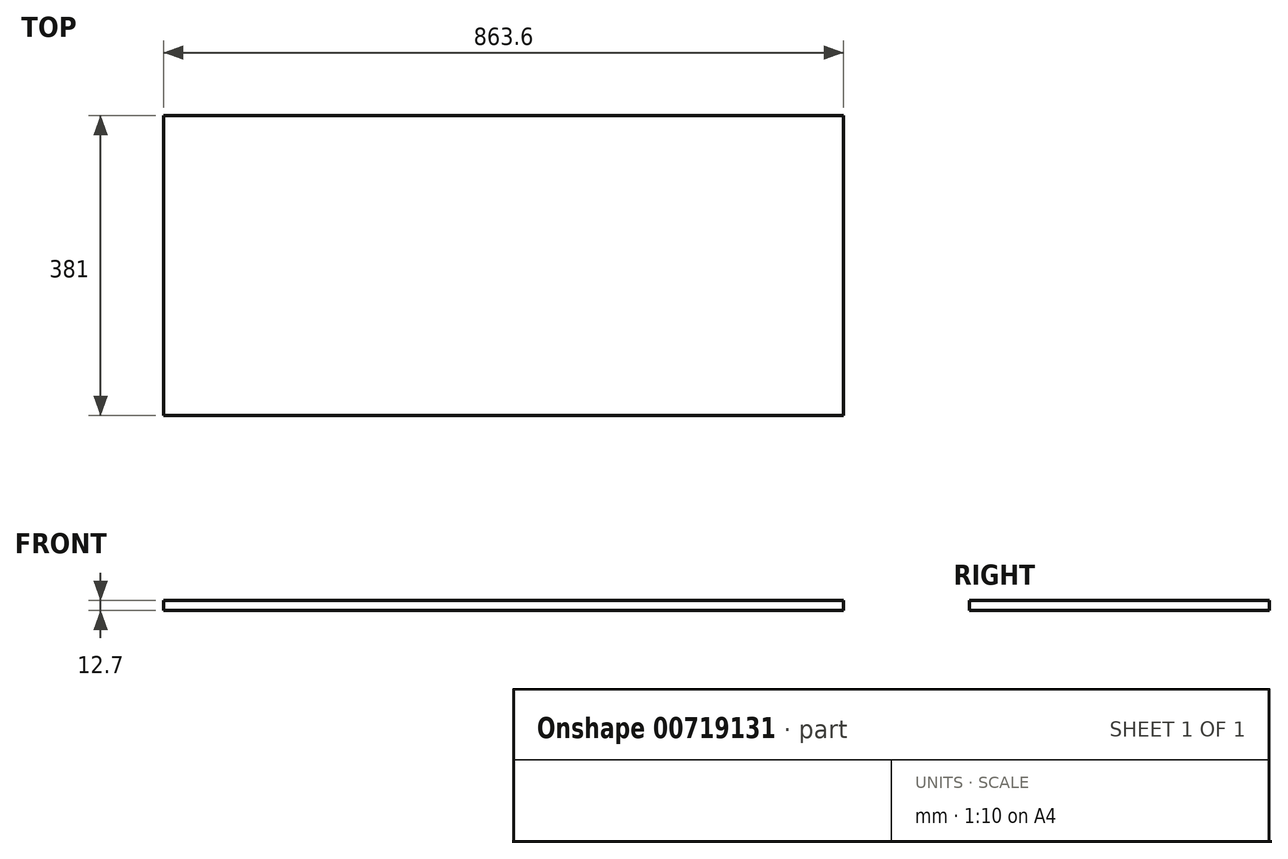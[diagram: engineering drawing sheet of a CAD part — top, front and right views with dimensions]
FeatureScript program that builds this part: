
annotation { "Feature Type Name" : "Feature", "Feature Type Description" : "" }
export const myFeature = defineFeature(function(context is Context, id is Id, definition is map)
    precondition{}
    {
        {
            var Q0;
            Q0=qCreatedBy(makeId("Top.planeOp"),FACE);
            var sketch = newSketch(context, id + "F0", { "sketchPlane" : qUnion([Q0])});
            skLineSegment(sketch, "E0.bottom", {"start": v(0, 0) * mm, "end": v(-863.6, 0) * mm});
            skLineSegment(sketch, "E0.top", {"start": v(0, 381) * mm, "end": v(-863.6, 381) * mm});
            skLineSegment(sketch, "E0.left", {"start": v(0, 0) * mm, "end": v(0, 381) * mm});
            skLineSegment(sketch, "E0.right", {"start": v(-863.6, 0) * mm, "end": v(-863.6, 381) * mm});
            skSolve(sketch);
        }
        {
            var Q0;
            Q0 = qSketchRegion(id + "F0", true);
            extrude(context, id + "F1", {"entities" : qUnion([Q0]), "depth" : 12.7 * mm, "offsetDistance" : 25.4 * mm});
        }
    });
